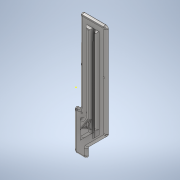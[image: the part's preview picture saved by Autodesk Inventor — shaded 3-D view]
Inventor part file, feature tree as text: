
AUTODESK INVENTOR PART (.ipt)
format: ipt  version: 2022 (Build 260153000, 153)  size: 602,112 bytes
history: native  units: in
note: dims shown in document units (in); Inventor stores cm internally (conversion verified against a paired STEP export)
features: sketch x15, extrude x14, projected_geometry x10, fillet x5
ambient origin geometry x8: Origin, YZ Plane, XZ Plane, XY Plane, X Axis, Y Axis, Z Axis, Center Point
bodies: Body1 (feature_tree)
feature tree (44):
  sketch  "Sketch1"  dims[d0=2.874in d1=1.1024in]
  extrude  "Extrusion2"  Depth=1.1024in
  extrude  "Extrusion3"  Depth=0.2559in
  extrude  "Extrusion4"  Depth=0.0049in
  extrude  "Extrusion5"  Depth=0.125in
  extrude  "Extrusion6"  Depth=1.102in
  fillet  "Fillet1"  Radius=2.0in
  sketch  "Sketch9"  dims[d8=135.0deg d10=1.102in d11=2.0in]
  extrude  "Extrusion10"  Depth=0.18in
  extrude  "Extrusion11"  Depth=0.3937in
  extrude  "Extrusion13"  Depth=0.125in TaperAngle=0.0deg
  sketch  "Sketch14"  dims[d29=0.125in d30=0.0in d31=1.3in d32=0.0in]
  extrude  "Extrusion16"  Depth=1.3in TaperAngle=0.0deg
  extrude  "Extrusion17"  Depth=0.125in TaperAngle=0.0deg
  extrude  "Extrusion19"  Depth=0.079in
  fillet  "Fillet2"  Radius=0.175in
  fillet  "Fillet3"  Radius=0.06in
  fillet  "Fillet4"  Radius=0.9in
  extrude  "Extrusion20"  Depth=0.25in
  extrude  "Extrusion21"  Depth=0.079in
  fillet  "Fillet5"  Radius=0.079in
  extrude  "Extrusion22"  Depth=0.079in
  sketch  "Sketch2"  dims[d2=0.1378in d3=0.2559in]
  projected_geometry  "Projected Loop1"
  sketch  "Sketch3"  dims[d4=0.2559in d5=0.0049in]
  projected_geometry  "Projected Loop2"
  projected_geometry  "Projected Loop3"
  projected_geometry  "Projected Loop4"
  sketch  "Sketch4"  dims[d6=0.125in d7=0.125in]
  sketch  "Sketch10"  dims[d17=0.18in d18=0.18in]
  sketch  "Sketch11"  dims[d21=0.18in d23=0.3937in]
  sketch  "Sketch13"  dims[d24=0.125in d27=0.125in d28=0.0in]
  projected_geometry  "Projected Loop7"
  sketch  "Sketch16"  dims[d33=0.9in d34=0.0in d35=0.125in d36=0.0in]
  projected_geometry  "Projected Loop9"
  sketch  "Sketch17"  dims[d37=0.135in d97=0.079in d98=0.175in d99=0.06in d100=0.0in d101=0.9in]
  sketch  "Sketch20"  dims[d102=1.6in d103=0.25in]
  projected_geometry  "Projected Loop12"
  sketch  "Sketch21"  dims[d104=0.0in d105=0.0in d114=0.079in d115=0.079in]
  projected_geometry  "Projected Loop13"
  sketch  "Sketch22"  dims[d116=0.079in d117=0.079in]
  projected_geometry  "Projected Loop14"
  sketch  "Sketch23"  dims[d118=0.079in d119=0.079in d120=0.079in d121=0.079in d122=0.5in d123=0.0in d124=0.12in d125=0.12in d126=0.12in d127=0.12in d128=0.4in d129=0.4in d130=0.6in d131=1.15in d136=1.0in d137=0.0in d138=1.3in d139=0.0in d142=0.4in d143=0.125in d144=0.0in d145=0.0625in d146=0.125in d147=0.125in d148=0.2in d149=0.29in d150=0.19in d151=0.0in d152=0.76in d153=0.125in d154=0.0in d155=0.125in d156=1.0in d157=0.0in]
  projected_geometry  "Projected Loop15"
